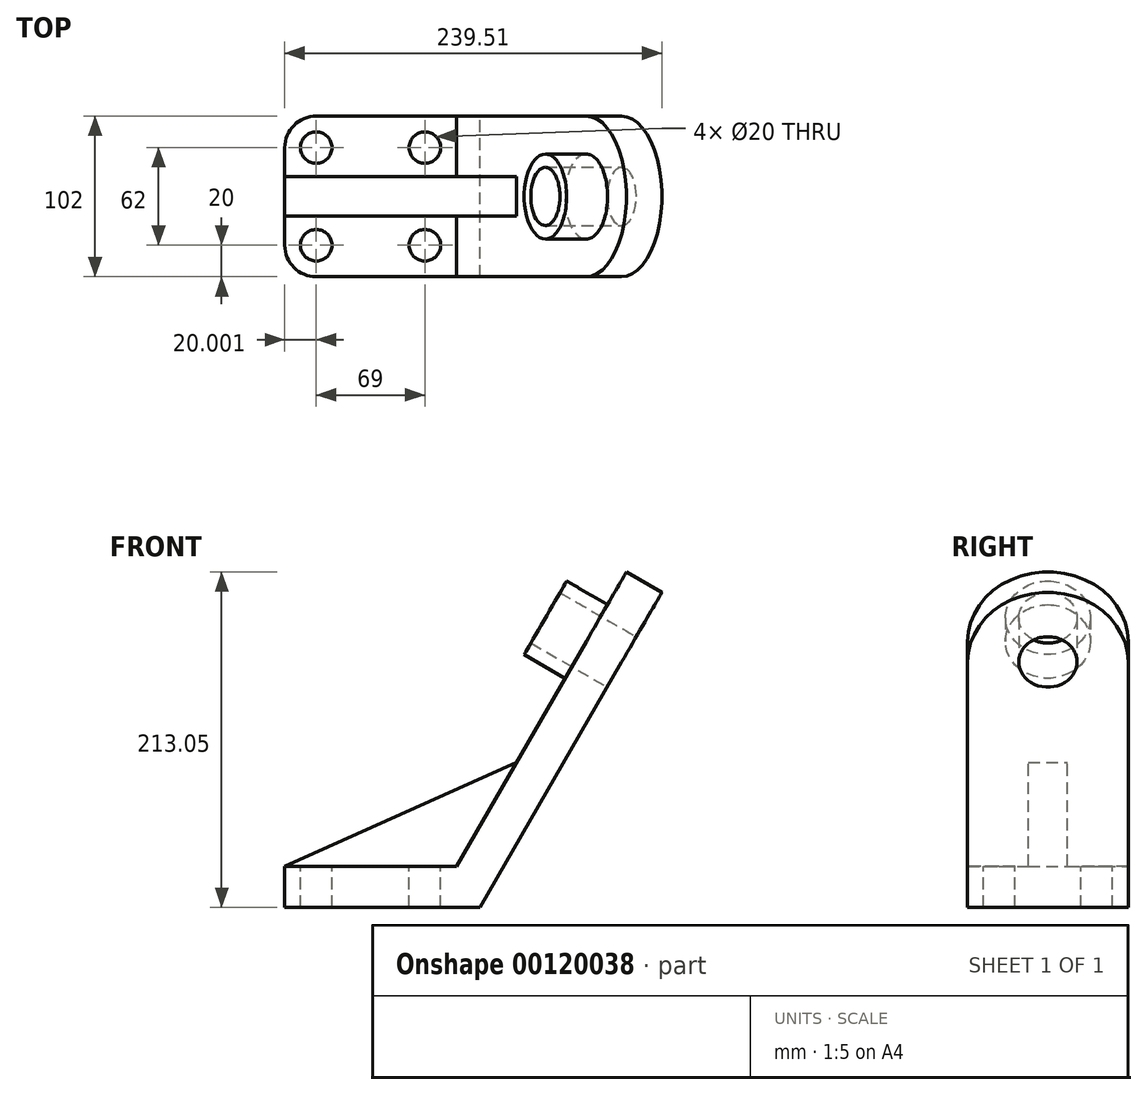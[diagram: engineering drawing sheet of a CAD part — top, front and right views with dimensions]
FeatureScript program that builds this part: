
annotation { "Feature Type Name" : "Feature", "Feature Type Description" : "" }
export const myFeature = defineFeature(function(context is Context, id is Id, definition is map)
    precondition{}
    {
        {
            var Q0;
            Q0=qCreatedBy(makeId("Front.planeOp"),FACE);
            var sketch = newSketch(context, id + "F0", { "sketchPlane" : qUnion([Q0])});
            skLineSegment(sketch, "E0", {"start": v(-145.3, -102.7) * mm, "end": v(-36.3, -102.7) * mm});
            skLineSegment(sketch, "E1", {"start": v(-36.3, -102.7) * mm, "end": v(71.7, 84.35) * mm});
            skLineSegment(sketch, "E2", {"start": v(-145.3, -102.7) * mm, "end": v(-145.3, -128.7) * mm});
            skLineSegment(sketch, "E3", {"start": v(-145.3, -128.7) * mm, "end": v(-21.29, -128.7) * mm});
            skLineSegment(sketch, "E4", {"start": v(-21.29, -128.7) * mm, "end": v(94.21, 71.35) * mm});
            skLineSegment(sketch, "E5", {"start": v(94.21, 71.35) * mm, "end": v(71.7, 84.35) * mm});
            skSolve(sketch);
        }
        {
            var Q0;
            Q0=makeQuery(id+"F0.imprint","IMPRINT",FACE,{"disambiguationData":[TD([[makeQuery(id+"F0.imprint","IMPRINT",EDGE,{"derivedFrom":sQuery(id+"F0.wireOp",EDGE,"E0")}),-1.0]])]});
            extrude(context, id + "F1", {"entities" : qUnion([Q0]), "depth" : 102 * mm});
        }
        {
            var Q0;
            Q0=makeQuery(id+"F1.opExtrude","CAP_EDGE",EDGE,{"disambiguationData":[OSD([sQuery(id+"F0.wireOp",EDGE,"E5")])],"isStart":true});
            var Q1;
            Q1=makeQuery(id+"F1.opExtrude","CAP_EDGE",EDGE,{"disambiguationData":[OSD([sQuery(id+"F0.wireOp",EDGE,"E5")])],"isStart":false});
            fillet(context, id + "F2", {"entities" : qUnion([Q0, Q1]), "radius" : 51 * mm, "tangentPropagation" : true, "allowEdgeOverflow" : false});
        }
        {
            var Q0;
            Q0=makeQuery(id+"F1.opExtrude","SWEPT_FACE",FACE,{"disambiguationData":[OSD([sQuery(id+"F0.wireOp",EDGE,"E1")])]});
            var sketch = newSketch(context, id + "F3", { "sketchPlane" : qUnion([Q0])});
            skLineSegment(sketch, "E6", {"start": v(102, 57.9) * mm, "end": v(0, 57.9) * mm, "construction": true});
            skCircle(sketch, "E7", {"center": v(51, 57.9) * mm, "radius": 27 * mm});
            skCircle(sketch, "E8", {"center": v(51, 57.9) * mm, "radius": 18.5 * mm});
            skSolve(sketch);
        }
        {
            var Q0;
            Q0 = qSketchRegion(id + "F3", true);
            extrude(context, id + "F4", {"entities" : qUnion([Q0]), "operationType" : NewBodyOperationType.ADD, "depth" : 30 * mm});
        }
        {
            var Q0;
            Q0=makeQuery(id+"F4.boolean.opBoolean","SPLIT",FACE,{"disambiguationData":[TD([makeQuery(id+"F4.opExtrude","SWEPT_FACE",FACE,{"disambiguationData":[OSD([sQuery(id+"F3.wireOp",EDGE,"E8")])]})])],"derivedFrom":makeQuery(id+"F1.opExtrude","SWEPT_FACE",FACE,{"disambiguationData":[OSD([sQuery(id+"F0.wireOp",EDGE,"E1")])]})});
            var sketch = newSketch(context, id + "F5", { "sketchPlane" : qUnion([Q0])});
            skCircle(sketch, "E9.0.0", {"center": v(51, 57.9) * mm, "radius": 18.5 * mm});
            skSolve(sketch);
        }
        {
            var Q0;
            Q0 = qSketchRegion(id + "F5", true);
            extrude(context, id + "F6", {"entities" : qUnion([Q0]), "operationType" : NewBodyOperationType.REMOVE, "oppositeDirection" : true, "depth" : 30 * mm});
        }
        {
            var Q0;
            Q0=makeQuery(id+"F1.opExtrude","SWEPT_FACE",FACE,{"disambiguationData":[OSD([sQuery(id+"F0.wireOp",EDGE,"E0")])]});
            var sketch = newSketch(context, id + "F7", { "sketchPlane" : qUnion([Q0])});
            skCircle(sketch, "E10", {"center": v(-125.3, -20) * mm, "radius": 10 * mm});
            skCircle(sketch, "E11.0.1.0", {"center": v(-125.3, -82) * mm, "radius": 10 * mm});
            skCircle(sketch, "E11.1.0.0", {"center": v(-56.3, -20) * mm, "radius": 10 * mm});
            skCircle(sketch, "E11.1.1.0", {"center": v(-56.3, -82) * mm, "radius": 10 * mm});
            skLineSegment(sketch, "E11.direction1", {"start": v(-125.3, -20) * mm, "end": v(-56.3, -20) * mm, "construction": true});
            skLineSegment(sketch, "E11.direction2", {"start": v(-125.3, -20) * mm, "end": v(-125.3, -82) * mm, "construction": true});
            skSolve(sketch);
        }
        {
            var Q0;
            Q0 = qSketchRegion(id + "F7", true);
            extrude(context, id + "F8", {"entities" : qUnion([Q0]), "operationType" : NewBodyOperationType.REMOVE, "oppositeDirection" : true, "depth" : 30 * mm});
        }
        {
            var Q0;
            Q0=makeQuery(id+"F1.opExtrude","CAP_FACE",FACE,{"disambiguationData":[OSD([sQuery(id+"F0.wireOp",EDGE,"E0"),sQuery(id+"F0.wireOp",EDGE,"E1"),sQuery(id+"F0.wireOp",EDGE,"E2"),sQuery(id+"F0.wireOp",EDGE,"E3"),sQuery(id+"F0.wireOp",EDGE,"E4"),sQuery(id+"F0.wireOp",EDGE,"E5")])],"isStart":false});
            cPlane(context, id + "F9", {"entities" : qUnion([Q0]), "cplaneType" : CPlaneType.OFFSET, "offset" : 51 * mm, "oppositeDirection" : true, "width" : 150 * mm, "height" : 150 * mm});
        }
        {
            var Q0;
            Q0=qCreatedBy(id+"F9.planeOp",FACE);
            var sketch = newSketch(context, id + "F10", { "sketchPlane" : qUnion([Q0])});
            skLineSegment(sketch, "E12", {"start": v(1.87, -36.6) * mm, "end": v(-145.3, -102.7) * mm});
            skLineSegment(sketch, "E13", {"start": v(-145.3, -102.7) * mm, "end": v(-35.63, -102.7) * mm});
            skLineSegment(sketch, "E14", {"start": v(-35.63, -102.7) * mm, "end": v(1.87, -36.6) * mm});
            skSolve(sketch);
        }
        {
            var Q0;
            Q0 = qSketchRegion(id + "F10", true);
            extrude(context, id + "F11", {"entities" : qUnion([Q0]), "operationType" : NewBodyOperationType.ADD, "endBound" : BoundingType.SYMMETRIC, "depth" : 25 * mm});
        }
        {
            var Q0;
            Q0=makeQuery(id+"F1.opExtrude","CAP_EDGE",EDGE,{"disambiguationData":[OSD([sQuery(id+"F0.wireOp",EDGE,"E2")])],"isStart":true});
            var Q1;
            Q1=makeQuery(id+"F1.opExtrude","CAP_EDGE",EDGE,{"disambiguationData":[OSD([sQuery(id+"F0.wireOp",EDGE,"E2")])],"isStart":false});
            fillet(context, id + "F12", {"entities" : qUnion([Q0, Q1]), "radius" : 20 * mm, "tangentPropagation" : true, "allowEdgeOverflow" : false});
        }
    });
